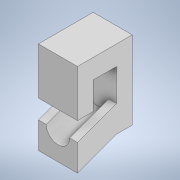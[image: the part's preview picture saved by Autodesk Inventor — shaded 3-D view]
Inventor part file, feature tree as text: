
AUTODESK INVENTOR PART (.ipt)
format: ipt  version: 2021 (Build 250183000, 183)  size: 158,208 bytes
history: native  units: mm
features: sketch x7, extrude x5, plane x1, sweep x1, thread x1
ambient origin geometry x8: Origin, YZ Plane, XZ Plane, XY Plane, X Axis, Y Axis, Z Axis, Center Point
bodies: Solid1 (feature_tree)
feature tree (15):
  extrude  "Extrusion1"  Depth=50.0mm
  extrude  "Extrusion2"  Depth=12.5mm
  extrude  "Extrusion3"  Depth=10.0mm
  extrude  "Extrusion4"  Depth=6.0mm TaperAngle=0.0deg
  extrude  "Extrusion5"  Depth=15.0mm TaperAngle=0.0deg
  sketch  "Sketch6"  dims[d14=25.0mm d15=10.0mm d16=0.0mm d17=15.0mm]
  plane  "Work Plane1"
  sweep  "Sweep1"
  thread  "Thread1"  [1 undecoded]
  sketch  "Sketch1"  dims[d0=25.0mm d1=50.0mm]
  sketch  "Sketch2"  dims[d2=12.5mm d3=12.5mm]
  sketch  "Sketch3"  dims[d4=10.0mm d5=0.0mm d7=3.0mm]
  sketch  "Sketch4"  dims[d8=33.0mm d9=6.0mm d10=0.0mm]
  sketch  "Sketch5"  dims[d11=15.0mm d12=15.0mm d13=0.0mm]
  sketch  "Sketch8"  dims[d18=15.0mm d19=10.0mm d20=0.0mm d21=30.0mm d22=15.0mm d23=17.0mm d24=17.0mm d25=-12.5mm d26=3.490659mm d27=8.5mm d28=0.0mm d29=0.0mm d30=6.0mm d31=0.0mm d32=25.0mm d33=0.872665mm d34=0.5mm d35=0.872665mm]
note: 1 required parameter value undecoded (feature->parameter linkage not recoverable at this tier; creation-order binding heuristic only, values carry confidence <= 0.55)
